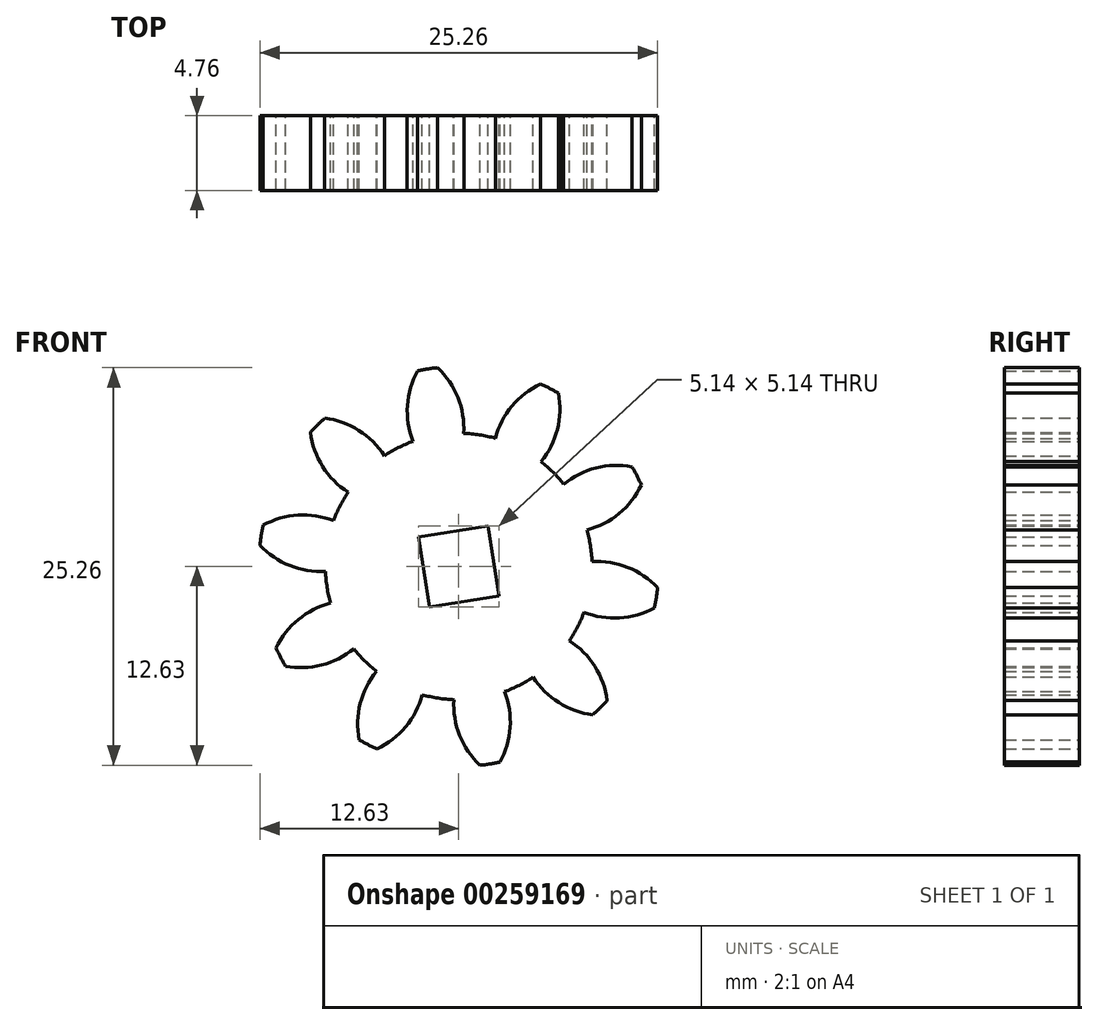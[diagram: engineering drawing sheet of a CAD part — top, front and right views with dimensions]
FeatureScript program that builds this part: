
annotation { "Feature Type Name" : "Feature", "Feature Type Description" : "" }
export const myFeature = defineFeature(function(context is Context, id is Id, definition is map)
    precondition{}
    {
        {
            var Q0;
            Q0=qCreatedBy(makeId("Front.planeOp"),FACE);
            var sketch = newSketch(context, id + "F0", { "sketchPlane" : qUnion([Q0])});
            skCircle(sketch, "E0", {"center": v(0, 0) * mm, "radius": 8.47 * mm});
            skCircle(sketch, "E1", {"center": v(0, 0) * mm, "radius": 10.58 * mm, "construction": true});
            skCircle(sketch, "E2", {"center": v(0, 0) * mm, "radius": 12.7 * mm, "construction": true});
            skLineSegment(sketch, "E3", {"start": v(0, 0) * mm, "end": v(0, 10.58) * mm, "construction": true});
            skLineSegment(sketch, "E4", {"start": v(0, 10.58) * mm, "end": v(-20.49, 10.58) * mm, "construction": true});
            skLineSegment(sketch, "E5", {"start": v(0, 10.58) * mm, "end": v(-19.5, 3.48) * mm, "construction": true});
            skLineSegment(sketch, "E6", {"start": v(0, 0) * mm, "end": v(-1.99, 12.54) * mm, "construction": true});
            skArc(sketch, "E7", {"start": v(0.27, 9.52) * mm, "mid": v(-0.28, 11.21) * mm, "end": v(-1.35, 12.63) * mm});
            skCircle(sketch, "E8", {"center": v(0, 0) * mm, "radius": 9.52 * mm, "construction": true});
            skArc(sketch, "E9.MirrorCS", {"start": v(-3.2, 8.97) * mm, "mid": v(-3.2, 10.75) * mm, "end": v(-2.62, 12.43) * mm});
            skArc(sketch, "E10", {"start": v(-1.35, 12.63) * mm, "mid": v(-1.99, 12.54) * mm, "end": v(-2.62, 12.43) * mm});
            skArc(sketch, "E11", {"start": v(0.3, 8.46) * mm, "mid": v(0.26, 9.54) * mm, "end": v(0, 10.58) * mm});
            skArc(sketch, "E12", {"start": v(-2.62, 12.43) * mm, "mid": v(-3.26, 10.22) * mm, "end": v(-2.9, 7.95) * mm});
            skCircle(sketch, "E13", {"center": v(0, 0) * mm, "radius": 3.18 * mm, "construction": true});
            skLineSegment(sketch, "E14", {"start": v(-2.57, 1.87) * mm, "end": v(1.87, 2.57) * mm});
            skLineSegment(sketch, "E15", {"start": v(1.87, 2.57) * mm, "end": v(2.57, -1.87) * mm});
            skLineSegment(sketch, "E16", {"start": v(2.57, -1.87) * mm, "end": v(-1.87, -2.57) * mm});
            skLineSegment(sketch, "E17", {"start": v(-1.87, -2.57) * mm, "end": v(-2.57, 1.87) * mm});
            skSolve(sketch);
        }
        {
            var Q0;
            Q0 = qSketchRegion(id + "F0", true);
            extrude(context, id + "F1", {"entities" : qUnion([Q0]), "depth" : 4.76 * mm});
        }
        {
            var Q0;
            Q0=makeQuery(id+"F1.opExtrude","SWEPT_FACE",FACE,{"disambiguationData":[OSD([sQuery(id+"F0.wireOp",EDGE,"E10")])]});
            var Q1;
            Q1=makeQuery(id+"F1.opExtrude","SWEPT_FACE",FACE,{"disambiguationData":[OSD([sQuery(id+"F0.wireOp",EDGE,"E7"),sQuery(id+"F0.wireOp",EDGE,"E11")])]});
            var Q2;
            Q2=makeQuery(id+"F1.opExtrude","SWEPT_FACE",FACE,{"disambiguationData":[OSD([sQuery(id+"F0.wireOp",EDGE,"E12")])]});
            var Q3;
            Q3=makeQuery(id+"F1.opExtrude","SWEPT_FACE",FACE,{"disambiguationData":[OSD([sQuery(id+"F0.wireOp",EDGE,"E0")])]});
            circularPattern(context, id + "F2", {"patternType" : PatternType.FACE, "faces" : qUnion([Q0, Q1, Q2]), "axis" : qUnion([Q3]), "angle" : 360 * degree, "instanceCount" : 10, "equalSpace" : true});
        }
    });
